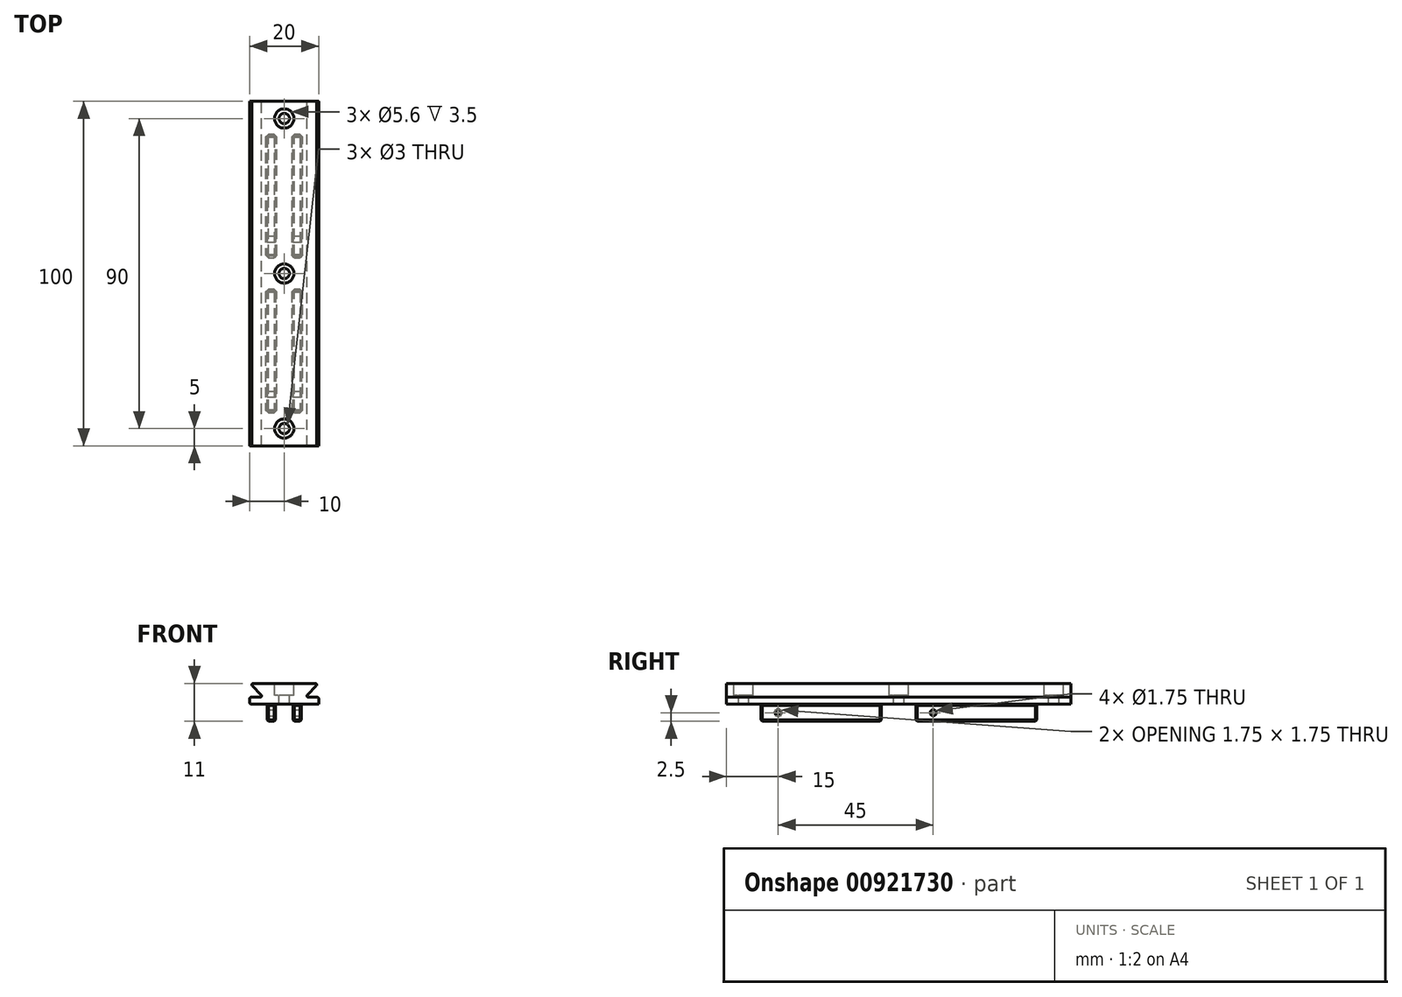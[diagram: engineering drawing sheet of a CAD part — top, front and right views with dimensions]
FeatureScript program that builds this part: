
annotation { "Feature Type Name" : "Feature", "Feature Type Description" : "" }
export const myFeature = defineFeature(function(context is Context, id is Id, definition is map)
    precondition{}
    {
        {
            var Q0;
            Q0=qCreatedBy(makeId("Front.planeOp"),FACE);
            var sketch = newSketch(context, id + "F0", { "sketchPlane" : qUnion([Q0])});
            skLineSegment(sketch, "E0.top", {"start": v(5, -2.5) * mm, "end": v(-5, -2.5) * mm});
            skLineSegment(sketch, "E0.left", {"start": v(5, 2.5) * mm, "end": v(5, -2.5) * mm});
            skLineSegment(sketch, "E0.right", {"start": v(-5, 2.5) * mm, "end": v(-5, -2.5) * mm});
            skPoint(sketch, "E0.middle", {"position": v(0, 0) * mm});
            skLineSegment(sketch, "E1.bottom", {"start": v(10, 4.5) * mm, "end": v(6, 4.5) * mm});
            skLineSegment(sketch, "E1.left", {"start": v(10, 4.5) * mm, "end": v(10, 2.5) * mm});
            skLineSegment(sketch, "E1.right", {"start": v(-10, 4.5) * mm, "end": v(-10, 2.5) * mm});
            skPoint(sketch, "E1.middle", {"position": v(0, 2.5) * mm});
            skLineSegment(sketch, "E2", {"start": v(-5, 2.5) * mm, "end": v(-10, 2.5) * mm});
            skLineSegment(sketch, "E3", {"start": v(5, 2.5) * mm, "end": v(10, 2.5) * mm});
            skPoint(sketch, "E4.orphan", {"position": v(-10, 0.5) * mm});
            skPoint(sketch, "E5.orphan", {"position": v(10, 0.5) * mm});
            skLineSegment(sketch, "E6.bottom", {"start": v(10, 8.5) * mm, "end": v(-10, 8.5) * mm});
            skPoint(sketch, "E6.middle", {"position": v(0, 4.5) * mm});
            skLineSegment(sketch, "E7.bottom", {"start": v(-10, 8.5) * mm, "end": v(-6, 8.5) * mm});
            skLineSegment(sketch, "E7.top", {"start": v(-10, 4.5) * mm, "end": v(-6, 4.5) * mm});
            skLineSegment(sketch, "E8.bottom", {"start": v(10, 8.5) * mm, "end": v(6, 8.5) * mm});
            skLineSegment(sketch, "E9", {"start": v(-10, 8.5) * mm, "end": v(-6, 4.5) * mm});
            skLineSegment(sketch, "E10", {"start": v(10, 8.5) * mm, "end": v(6, 4.5) * mm});
            skLineSegment(sketch, "E11.trimOffspring", {"start": v(-6, 4.5) * mm, "end": v(-10, 4.5) * mm});
            skLineSegment(sketch, "E12.bottom", {"start": v(-2.5, -2.5) * mm, "end": v(2.5, -2.5) * mm});
            skLineSegment(sketch, "E12.top", {"start": v(-2.5, 2.5) * mm, "end": v(2.5, 2.5) * mm});
            skLineSegment(sketch, "E12.left", {"start": v(-2.5, -2.5) * mm, "end": v(-2.5, 2.5) * mm});
            skLineSegment(sketch, "E12.right", {"start": v(2.5, -2.5) * mm, "end": v(2.5, 2.5) * mm});
            skSolve(sketch);
        }
        {
            var Q0;
            {var subQ0=sQuery(id+"F0.wireOp",EDGE,"E0.left");Q0=makeQuery(id+"F0.imprint","IMPRINT",FACE,{"disambiguationData":[TD([[makeQuery(id+"F0.imprint","IMPRINT",EDGE,{"derivedFrom":subQ0}),-1.0]])]});}
            extrude(context, id + "F1", {"entities" : qUnion([Q0]), "depth" : 100 * mm, "offsetDistance" : 25 * mm});
        }
        {
            var Q0;
            Q0=makeQuery(id+"F1.opExtrude","SWEPT_FACE",FACE,{"disambiguationData":[OSD([sQuery(id+"F0.wireOp",EDGE,"E12.top")])]});
            var sketch = newSketch(context, id + "F2", { "sketchPlane" : qUnion([Q0])});
            skLineSegment(sketch, "E13", {"start": v(-2.5, 10) * mm, "end": v(2.5, 10) * mm});
            skLineSegment(sketch, "E14", {"start": v(2.5, 90) * mm, "end": v(-2.5, 90) * mm});
            skLineSegment(sketch, "E15.top", {"start": v(-2.5, 55) * mm, "end": v(2.5, 55) * mm});
            skLineSegment(sketch, "E15.left", {"start": v(-2.5, 50) * mm, "end": v(-2.5, 55) * mm});
            skLineSegment(sketch, "E15.right", {"start": v(2.5, 50) * mm, "end": v(2.5, 55) * mm});
            skLineSegment(sketch, "E16.top", {"start": v(2.5, 45) * mm, "end": v(-2.5, 45) * mm});
            skLineSegment(sketch, "E16.left", {"start": v(2.5, 50) * mm, "end": v(2.5, 45) * mm});
            skLineSegment(sketch, "E16.right", {"start": v(-2.5, 50) * mm, "end": v(-2.5, 45) * mm});
            skSolve(sketch);
        }
        {
            var Q0;
            {var subQ0=sQuery(id+"F2.wireOp",EDGE,"E14");Q0=makeQuery(id+"F2.imprint","IMPRINT",FACE,{"disambiguationData":[TD([[makeQuery(id+"F2.imprint","IMPRINT",EDGE,{"derivedFrom":subQ0}),-1.0]])]});}
            var Q1;
            Q1=makeQuery(id+"F2.imprint","IMPRINT",FACE,{"disambiguationData":[TD([[makeQuery(id+"F2.imprint","IMPRINT",EDGE,{"derivedFrom":sQuery(id+"F2.wireOp",EDGE,"E15.top")}),-1.0]])]});
            var Q2;
            {var subQ0=sQuery(id+"F2.wireOp",EDGE,"E13");Q2=makeQuery(id+"F2.imprint","IMPRINT",FACE,{"disambiguationData":[TD([[makeQuery(id+"F2.imprint","IMPRINT",EDGE,{"derivedFrom":subQ0}),-1.0]])]});}
            extrude(context, id + "F3", {"entities" : qUnion([Q0, Q1, Q2]), "operationType" : NewBodyOperationType.ADD, "depth" : 5 * mm, "offsetDistance" : 25 * mm});
        }
        {
            var Q0;
            Q0=makeQuery(id+"F1.opExtrude","SWEPT_FACE",FACE,{"disambiguationData":[OSD([sQuery(id+"F0.wireOp",EDGE,"E0.left")])]});
            var sketch = newSketch(context, id + "F4", { "sketchPlane" : qUnion([Q0])});
            skLineSegment(sketch, "E17", {"start": v(-100, 2.5) * mm, "end": v(-100, -19) * mm});
            skLineSegment(sketch, "E18", {"start": v(-100, -19) * mm, "end": v(0, -19) * mm});
            skLineSegment(sketch, "E19", {"start": v(0, -19) * mm, "end": v(0, 2.5) * mm});
            skCircle(sketch, "E20", {"center": v(-85, 0) * mm, "radius": 0.87 * mm});
            skCircle(sketch, "E21", {"center": v(-40, 0) * mm, "radius": 0.87 * mm});
            skSolve(sketch);
        }
        {
            var Q0;
            Q0 = qSketchRegion(id + "F4", true);
            extrude(context, id + "F5", {"entities" : qUnion([Q0]), "operationType" : NewBodyOperationType.REMOVE, "oppositeDirection" : true, "depth" : 25 * mm, "offsetDistance" : 25 * mm});
        }
        {
            var Q0;
            Q0=makeQuery(id+"F1.opExtrude","SWEPT_EDGE",EDGE,{"disambiguationData":[OSD([sQuery(id+"F0.wireOp",EDGE,"E1.left"),sQuery(id+"F0.wireOp",EDGE,"E1.bottom")])]});
            var Q1;
            Q1=makeQuery(id+"F1.opExtrude","SWEPT_EDGE",EDGE,{"disambiguationData":[OSD([sQuery(id+"F0.wireOp",EDGE,"E1.right"),sQuery(id+"F0.wireOp",EDGE,"E11.trimOffspring")])]});
            var Q2;
            Q2=makeQuery(id+"F1.opExtrude","SWEPT_EDGE",EDGE,{"disambiguationData":[OSD([sQuery(id+"F0.wireOp",EDGE,"E9"),sQuery(id+"F0.wireOp",EDGE,"E11.trimOffspring")])]});
            var Q3;
            Q3=makeQuery(id+"F1.opExtrude","SWEPT_EDGE",EDGE,{"disambiguationData":[OSD([sQuery(id+"F0.wireOp",EDGE,"E1.bottom"),sQuery(id+"F0.wireOp",EDGE,"E10")])]});
            var Q4;
            Q4=makeQuery(id+"F1.opExtrude","SWEPT_EDGE",EDGE,{"disambiguationData":[OSD([sQuery(id+"F0.wireOp",EDGE,"E8.bottom"),sQuery(id+"F0.wireOp",EDGE,"E10")])]});
            var Q5;
            Q5=makeQuery(id+"F1.opExtrude","SWEPT_EDGE",EDGE,{"disambiguationData":[OSD([sQuery(id+"F0.wireOp",EDGE,"E7.bottom"),sQuery(id+"F0.wireOp",EDGE,"E9")])]});
            fillet(context, id + "F6", {"entities" : qUnion([Q0, Q1, Q2, Q3, Q4, Q5]), "radius" : 0.4 * mm, "tangentPropagation" : true, "allowEdgeOverflow" : false});
        }
        {
            var Q0;
            Q0=makeQuery(id+"F1.opExtrude","SWEPT_FACE",FACE,{"disambiguationData":[OSD([sQuery(id+"F0.wireOp",EDGE,"E6.bottom"),sQuery(id+"F0.wireOp",EDGE,"E7.bottom"),sQuery(id+"F0.wireOp",EDGE,"E8.bottom")])]});
            var sketch = newSketch(context, id + "F7", { "sketchPlane" : qUnion([Q0])});
            skLineSegment(sketch, "E22", {"start": v(0, -100) * mm, "end": v(0, -95) * mm});
            skLineSegment(sketch, "E23", {"start": v(0, 0) * mm, "end": v(0, -5) * mm});
            skLineSegment(sketch, "E24", {"start": v(0, -5) * mm, "end": v(0, -95) * mm});
            skCircle(sketch, "E25", {"center": v(0, -50) * mm, "radius": 2.8 * mm});
            skCircle(sketch, "E26", {"center": v(0, -5) * mm, "radius": 2.8 * mm});
            skCircle(sketch, "E27", {"center": v(0, -95) * mm, "radius": 2.8 * mm});
            skCircle(sketch, "E28", {"center": v(0, -5) * mm, "radius": 1.5 * mm});
            skCircle(sketch, "E29", {"center": v(0, -50) * mm, "radius": 1.5 * mm});
            skCircle(sketch, "E30", {"center": v(0, -95) * mm, "radius": 1.5 * mm});
            skSolve(sketch);
        }
        {
            var Q0;
            Q0 = qSketchRegion(id + "F7", true);
            extrude(context, id + "F8", {"entities" : qUnion([Q0]), "operationType" : NewBodyOperationType.REMOVE, "oppositeDirection" : true, "depth" : 3.5 * mm, "offsetDistance" : 25 * mm});
        }
        {
            var Q0;
            Q0=makeQuery(id+"F8.boolean.opBoolean","SPLIT",FACE,{"disambiguationData":[TD([makeQuery(id+"F8.opExtrude","SWEPT_FACE",FACE,{"disambiguationData":[OSD([sQuery(id+"F7.wireOp",EDGE,"E28")])]})])],"derivedFrom":makeQuery(id+"F1.opExtrude","SWEPT_FACE",FACE,{"disambiguationData":[OSD([sQuery(id+"F0.wireOp",EDGE,"E6.bottom"),sQuery(id+"F0.wireOp",EDGE,"E7.bottom"),sQuery(id+"F0.wireOp",EDGE,"E8.bottom")])]})});
            var Q1;
            Q1=makeQuery(id+"F8.boolean.opBoolean","SPLIT",FACE,{"disambiguationData":[TD([makeQuery(id+"F8.opExtrude","SWEPT_FACE",FACE,{"disambiguationData":[OSD([sQuery(id+"F7.wireOp",EDGE,"E29")])]})])],"derivedFrom":makeQuery(id+"F1.opExtrude","SWEPT_FACE",FACE,{"disambiguationData":[OSD([sQuery(id+"F0.wireOp",EDGE,"E6.bottom"),sQuery(id+"F0.wireOp",EDGE,"E7.bottom"),sQuery(id+"F0.wireOp",EDGE,"E8.bottom")])]})});
            var Q2;
            Q2=makeQuery(id+"F8.boolean.opBoolean","SPLIT",FACE,{"disambiguationData":[TD([makeQuery(id+"F8.opExtrude","SWEPT_FACE",FACE,{"disambiguationData":[OSD([sQuery(id+"F7.wireOp",EDGE,"E30")])]})])],"derivedFrom":makeQuery(id+"F1.opExtrude","SWEPT_FACE",FACE,{"disambiguationData":[OSD([sQuery(id+"F0.wireOp",EDGE,"E6.bottom"),sQuery(id+"F0.wireOp",EDGE,"E7.bottom"),sQuery(id+"F0.wireOp",EDGE,"E8.bottom")])]})});
            extrude(context, id + "F9", {"entities" : qUnion([Q0, Q1, Q2]), "operationType" : NewBodyOperationType.REMOVE, "endBound" : BoundingType.THROUGH_ALL, "oppositeDirection" : true, "depth" : 25 * mm, "offsetDistance" : 25 * mm});
        }
        {
            var Q0;
            Q0=makeQuery(id+"F8.boolean.opBoolean","COPY",EDGE,{"derivedFrom":makeQuery(id+"F8.opExtrude","CAP_EDGE",EDGE,{"disambiguationData":[OSD([sQuery(id+"F7.wireOp",EDGE,"E26")])],"isStart":true})});
            var Q1;
            Q1=makeQuery(id+"F8.boolean.opBoolean","COPY",EDGE,{"derivedFrom":makeQuery(id+"F8.opExtrude","CAP_EDGE",EDGE,{"disambiguationData":[OSD([sQuery(id+"F7.wireOp",EDGE,"E25")])],"isStart":true})});
            var Q2;
            Q2=makeQuery(id+"F8.boolean.opBoolean","COPY",EDGE,{"derivedFrom":makeQuery(id+"F8.opExtrude","CAP_EDGE",EDGE,{"disambiguationData":[OSD([sQuery(id+"F7.wireOp",EDGE,"E27")])],"isStart":true})});
            var Q3;
            Q3=makeQuery(id+"F8.boolean.opBoolean","COPY",EDGE,{"derivedFrom":makeQuery(id+"F8.opExtrude","CAP_EDGE",EDGE,{"disambiguationData":[OSD([sQuery(id+"F7.wireOp",EDGE,"E28")])],"isStart":false})});
            var Q4;
            Q4=makeQuery(id+"F8.boolean.opBoolean","COPY",EDGE,{"derivedFrom":makeQuery(id+"F8.opExtrude","CAP_EDGE",EDGE,{"disambiguationData":[OSD([sQuery(id+"F7.wireOp",EDGE,"E29")])],"isStart":false})});
            var Q5;
            Q5=makeQuery(id+"F8.boolean.opBoolean","COPY",EDGE,{"derivedFrom":makeQuery(id+"F8.opExtrude","CAP_EDGE",EDGE,{"disambiguationData":[OSD([sQuery(id+"F7.wireOp",EDGE,"E30")])],"isStart":false})});
            var Q6;
            {var subQ0=sQuery(id+"F0.wireOp",EDGE,"E12.right");var subQ1=sQuery(id+"F0.wireOp",EDGE,"E12.left");var subQ2=sQuery(id+"F0.wireOp",EDGE,"E12.top");var subQ3=sQuery(id+"F0.wireOp",EDGE,"E0.top");Q6=makeQuery(id+"F9.boolean.opBoolean","INTERSECT",EDGE,{"derivedFrom":[makeQuery(id+"F3.boolean.opBoolean","MERGE",FACE,{"derivedFrom":[makeQuery(id+"F1.opExtrude","SWEPT_FACE",FACE,{"disambiguationData":[OSD([subQ3]),TDD([makeQuery(id+"F0.imprint","IMPRINT",EDGE,{"disambiguationData":[TD([[makeQuery(id+"F0.imprint","INTERSECT",VERTEX,{"derivedFrom":[subQ3,sQuery(id+"F0.wireOp",EDGE,"E0.left")]}),-1.0]])],"derivedFrom":subQ3})])]}),makeQuery(id+"F1.opExtrude","SWEPT_FACE",FACE,{"disambiguationData":[OSD([subQ3]),TDD([makeQuery(id+"F0.imprint","IMPRINT",EDGE,{"disambiguationData":[TD([[makeQuery(id+"F0.imprint","INTERSECT",VERTEX,{"derivedFrom":[subQ3,sQuery(id+"F0.wireOp",EDGE,"E0.right")]}),1.0]])],"derivedFrom":subQ3})])]}),makeQuery(id+"F3.opExtrude","CAP_FACE",FACE,{"disambiguationData":[OSD([subQ2,subQ1,subQ0,sQuery(id+"F2.wireOp",EDGE,"E13")])],"isStart":false}),makeQuery(id+"F3.opExtrude","CAP_FACE",FACE,{"disambiguationData":[OSD([subQ2,subQ1,subQ0,sQuery(id+"F2.wireOp",EDGE,"E14")])],"isStart":false}),makeQuery(id+"F3.opExtrude","CAP_FACE",FACE,{"disambiguationData":[OSD([sQuery(id+"F2.wireOp",EDGE,"E15.top"),sQuery(id+"F2.wireOp",EDGE,"E15.left"),sQuery(id+"F2.wireOp",EDGE,"E15.right"),sQuery(id+"F2.wireOp",EDGE,"E16.top"),sQuery(id+"F2.wireOp",EDGE,"E16.left"),sQuery(id+"F2.wireOp",EDGE,"E16.right")])],"isStart":false})]}),makeQuery(id+"F9.opExtrude","SWEPT_FACE",FACE,{"disambiguationData":[OSD([sQuery(id+"F7.wireOp",EDGE,"E30")])]})]});}
            var Q7;
            {var subQ0=sQuery(id+"F0.wireOp",EDGE,"E12.right");var subQ1=sQuery(id+"F0.wireOp",EDGE,"E12.left");var subQ2=sQuery(id+"F0.wireOp",EDGE,"E12.top");var subQ3=sQuery(id+"F0.wireOp",EDGE,"E0.top");Q7=makeQuery(id+"F9.boolean.opBoolean","INTERSECT",EDGE,{"derivedFrom":[makeQuery(id+"F3.boolean.opBoolean","MERGE",FACE,{"derivedFrom":[makeQuery(id+"F1.opExtrude","SWEPT_FACE",FACE,{"disambiguationData":[OSD([subQ3]),TDD([makeQuery(id+"F0.imprint","IMPRINT",EDGE,{"disambiguationData":[TD([[makeQuery(id+"F0.imprint","INTERSECT",VERTEX,{"derivedFrom":[subQ3,sQuery(id+"F0.wireOp",EDGE,"E0.left")]}),-1.0]])],"derivedFrom":subQ3})])]}),makeQuery(id+"F1.opExtrude","SWEPT_FACE",FACE,{"disambiguationData":[OSD([subQ3]),TDD([makeQuery(id+"F0.imprint","IMPRINT",EDGE,{"disambiguationData":[TD([[makeQuery(id+"F0.imprint","INTERSECT",VERTEX,{"derivedFrom":[subQ3,sQuery(id+"F0.wireOp",EDGE,"E0.right")]}),1.0]])],"derivedFrom":subQ3})])]}),makeQuery(id+"F3.opExtrude","CAP_FACE",FACE,{"disambiguationData":[OSD([subQ2,subQ1,subQ0,sQuery(id+"F2.wireOp",EDGE,"E13")])],"isStart":false}),makeQuery(id+"F3.opExtrude","CAP_FACE",FACE,{"disambiguationData":[OSD([subQ2,subQ1,subQ0,sQuery(id+"F2.wireOp",EDGE,"E14")])],"isStart":false}),makeQuery(id+"F3.opExtrude","CAP_FACE",FACE,{"disambiguationData":[OSD([sQuery(id+"F2.wireOp",EDGE,"E15.top"),sQuery(id+"F2.wireOp",EDGE,"E15.left"),sQuery(id+"F2.wireOp",EDGE,"E15.right"),sQuery(id+"F2.wireOp",EDGE,"E16.top"),sQuery(id+"F2.wireOp",EDGE,"E16.left"),sQuery(id+"F2.wireOp",EDGE,"E16.right")])],"isStart":false})]}),makeQuery(id+"F9.opExtrude","SWEPT_FACE",FACE,{"disambiguationData":[OSD([sQuery(id+"F7.wireOp",EDGE,"E29")])]})]});}
            var Q8;
            {var subQ0=sQuery(id+"F0.wireOp",EDGE,"E12.right");var subQ1=sQuery(id+"F0.wireOp",EDGE,"E12.left");var subQ2=sQuery(id+"F0.wireOp",EDGE,"E12.top");var subQ3=sQuery(id+"F0.wireOp",EDGE,"E0.top");Q8=makeQuery(id+"F9.boolean.opBoolean","INTERSECT",EDGE,{"derivedFrom":[makeQuery(id+"F3.boolean.opBoolean","MERGE",FACE,{"derivedFrom":[makeQuery(id+"F1.opExtrude","SWEPT_FACE",FACE,{"disambiguationData":[OSD([subQ3]),TDD([makeQuery(id+"F0.imprint","IMPRINT",EDGE,{"disambiguationData":[TD([[makeQuery(id+"F0.imprint","INTERSECT",VERTEX,{"derivedFrom":[subQ3,sQuery(id+"F0.wireOp",EDGE,"E0.left")]}),-1.0]])],"derivedFrom":subQ3})])]}),makeQuery(id+"F1.opExtrude","SWEPT_FACE",FACE,{"disambiguationData":[OSD([subQ3]),TDD([makeQuery(id+"F0.imprint","IMPRINT",EDGE,{"disambiguationData":[TD([[makeQuery(id+"F0.imprint","INTERSECT",VERTEX,{"derivedFrom":[subQ3,sQuery(id+"F0.wireOp",EDGE,"E0.right")]}),1.0]])],"derivedFrom":subQ3})])]}),makeQuery(id+"F3.opExtrude","CAP_FACE",FACE,{"disambiguationData":[OSD([subQ2,subQ1,subQ0,sQuery(id+"F2.wireOp",EDGE,"E13")])],"isStart":false}),makeQuery(id+"F3.opExtrude","CAP_FACE",FACE,{"disambiguationData":[OSD([subQ2,subQ1,subQ0,sQuery(id+"F2.wireOp",EDGE,"E14")])],"isStart":false}),makeQuery(id+"F3.opExtrude","CAP_FACE",FACE,{"disambiguationData":[OSD([sQuery(id+"F2.wireOp",EDGE,"E15.top"),sQuery(id+"F2.wireOp",EDGE,"E15.left"),sQuery(id+"F2.wireOp",EDGE,"E15.right"),sQuery(id+"F2.wireOp",EDGE,"E16.top"),sQuery(id+"F2.wireOp",EDGE,"E16.left"),sQuery(id+"F2.wireOp",EDGE,"E16.right")])],"isStart":false})]}),makeQuery(id+"F9.opExtrude","SWEPT_FACE",FACE,{"disambiguationData":[OSD([sQuery(id+"F7.wireOp",EDGE,"E28")])]})]});}
            chamfer(context, id + "F10", {"entities" : qUnion([Q0, Q1, Q2, Q3, Q4, Q5, Q6, Q7, Q8]), "width" : 0.5 * mm, "tangentPropagation" : true});
        }
        {
            var Q0;
            Q0=makeQuery(id+"F1.opExtrude","SWEPT_FACE",FACE,{"disambiguationData":[OSD([sQuery(id+"F0.wireOp",EDGE,"E0.right")])]});
            var sketch = newSketch(context, id + "F11", { "sketchPlane" : qUnion([Q0])});
            skLineSegment(sketch, "E31.bottom", {"start": v(0, 2.5) * mm, "end": v(10, 2.5) * mm});
            skLineSegment(sketch, "E31.top", {"start": v(0, -2.5) * mm, "end": v(10, -2.5) * mm});
            skLineSegment(sketch, "E31.left", {"start": v(0, 2.5) * mm, "end": v(0, -2.5) * mm});
            skLineSegment(sketch, "E31.right", {"start": v(10, 2.5) * mm, "end": v(10, -2.5) * mm});
            skLineSegment(sketch, "E32.bottom", {"start": v(45, 2.5) * mm, "end": v(55, 2.5) * mm});
            skLineSegment(sketch, "E32.top", {"start": v(45, -2.5) * mm, "end": v(55, -2.5) * mm});
            skLineSegment(sketch, "E32.left", {"start": v(45, 2.5) * mm, "end": v(45, -2.5) * mm});
            skLineSegment(sketch, "E32.right", {"start": v(55, 2.5) * mm, "end": v(55, -2.5) * mm});
            skLineSegment(sketch, "E33.bottom", {"start": v(100, 2.5) * mm, "end": v(90, 2.5) * mm});
            skLineSegment(sketch, "E33.top", {"start": v(100, -2.5) * mm, "end": v(90, -2.5) * mm});
            skLineSegment(sketch, "E33.left", {"start": v(100, 2.5) * mm, "end": v(100, -2.5) * mm});
            skLineSegment(sketch, "E33.right", {"start": v(90, 2.5) * mm, "end": v(90, -2.5) * mm});
            skSolve(sketch);
        }
        {
            var Q0;
            Q0 = qSketchRegion(id + "F11", true);
            extrude(context, id + "F12", {"entities" : qUnion([Q0]), "operationType" : NewBodyOperationType.REMOVE, "oppositeDirection" : true, "depth" : 25 * mm, "offsetDistance" : 25 * mm});
        }
        {
            var Q0;
            {var subQ0=sQuery(id+"F0.wireOp",EDGE,"E0.left");var subQ1=sQuery(id+"F0.wireOp",EDGE,"E12.right");var subQ2=sQuery(id+"F0.wireOp",EDGE,"E12.left");var subQ3=sQuery(id+"F0.wireOp",EDGE,"E12.top");var subQ4=sQuery(id+"F0.wireOp",EDGE,"E0.top");Q0=makeQuery(id+"F12.boolean.opBoolean","SPLIT",FACE,{"disambiguationData":[TD([makeQuery(id+"F1.opExtrude","SWEPT_FACE",FACE,{"disambiguationData":[OSD([subQ0])]}),makeQuery(id+"F1.opExtrude","SWEPT_FACE",FACE,{"disambiguationData":[OSD([subQ1])]}),makeQuery(id+"F12.opExtrude","SWEPT_FACE",FACE,{"disambiguationData":[OSD([sQuery(id+"F11.wireOp",EDGE,"E32.right")])]}),makeQuery(id+"F12.opExtrude","SWEPT_FACE",FACE,{"disambiguationData":[OSD([sQuery(id+"F11.wireOp",EDGE,"E33.right")])]})])],"derivedFrom":makeQuery(id+"F3.boolean.opBoolean","MERGE",FACE,{"derivedFrom":[makeQuery(id+"F1.opExtrude","SWEPT_FACE",FACE,{"disambiguationData":[OSD([subQ4]),TDD([makeQuery(id+"F0.imprint","IMPRINT",EDGE,{"disambiguationData":[TD([[makeQuery(id+"F0.imprint","INTERSECT",VERTEX,{"derivedFrom":[subQ4,subQ0]}),-1.0]])],"derivedFrom":subQ4})])]}),makeQuery(id+"F1.opExtrude","SWEPT_FACE",FACE,{"disambiguationData":[OSD([subQ4]),TDD([makeQuery(id+"F0.imprint","IMPRINT",EDGE,{"disambiguationData":[TD([[makeQuery(id+"F0.imprint","INTERSECT",VERTEX,{"derivedFrom":[subQ4,sQuery(id+"F0.wireOp",EDGE,"E0.right")]}),1.0]])],"derivedFrom":subQ4})])]}),makeQuery(id+"F3.opExtrude","CAP_FACE",FACE,{"disambiguationData":[OSD([subQ3,subQ2,subQ1,sQuery(id+"F2.wireOp",EDGE,"E13")])],"isStart":false}),makeQuery(id+"F3.opExtrude","CAP_FACE",FACE,{"disambiguationData":[OSD([subQ3,subQ2,subQ1,sQuery(id+"F2.wireOp",EDGE,"E14")])],"isStart":false}),makeQuery(id+"F3.opExtrude","CAP_FACE",FACE,{"disambiguationData":[OSD([sQuery(id+"F2.wireOp",EDGE,"E15.top"),sQuery(id+"F2.wireOp",EDGE,"E15.left"),sQuery(id+"F2.wireOp",EDGE,"E15.right"),sQuery(id+"F2.wireOp",EDGE,"E16.top"),sQuery(id+"F2.wireOp",EDGE,"E16.left"),sQuery(id+"F2.wireOp",EDGE,"E16.right")])],"isStart":false})]})});}
            var Q1;
            {var subQ0=sQuery(id+"F0.wireOp",EDGE,"E0.right");var subQ1=sQuery(id+"F0.wireOp",EDGE,"E12.left");var subQ2=sQuery(id+"F0.wireOp",EDGE,"E12.right");var subQ3=sQuery(id+"F0.wireOp",EDGE,"E12.top");var subQ4=sQuery(id+"F0.wireOp",EDGE,"E0.top");Q1=makeQuery(id+"F12.boolean.opBoolean","SPLIT",FACE,{"disambiguationData":[TD([makeQuery(id+"F1.opExtrude","SWEPT_FACE",FACE,{"disambiguationData":[OSD([subQ0])]}),makeQuery(id+"F1.opExtrude","SWEPT_FACE",FACE,{"disambiguationData":[OSD([subQ1])]}),makeQuery(id+"F12.opExtrude","SWEPT_FACE",FACE,{"disambiguationData":[OSD([sQuery(id+"F11.wireOp",EDGE,"E32.right")])]}),makeQuery(id+"F12.opExtrude","SWEPT_FACE",FACE,{"disambiguationData":[OSD([sQuery(id+"F11.wireOp",EDGE,"E33.right")])]})])],"derivedFrom":makeQuery(id+"F3.boolean.opBoolean","MERGE",FACE,{"derivedFrom":[makeQuery(id+"F1.opExtrude","SWEPT_FACE",FACE,{"disambiguationData":[OSD([subQ4]),TDD([makeQuery(id+"F0.imprint","IMPRINT",EDGE,{"disambiguationData":[TD([[makeQuery(id+"F0.imprint","INTERSECT",VERTEX,{"derivedFrom":[subQ4,sQuery(id+"F0.wireOp",EDGE,"E0.left")]}),-1.0]])],"derivedFrom":subQ4})])]}),makeQuery(id+"F1.opExtrude","SWEPT_FACE",FACE,{"disambiguationData":[OSD([subQ4]),TDD([makeQuery(id+"F0.imprint","IMPRINT",EDGE,{"disambiguationData":[TD([[makeQuery(id+"F0.imprint","INTERSECT",VERTEX,{"derivedFrom":[subQ4,subQ0]}),1.0]])],"derivedFrom":subQ4})])]}),makeQuery(id+"F3.opExtrude","CAP_FACE",FACE,{"disambiguationData":[OSD([subQ3,subQ1,subQ2,sQuery(id+"F2.wireOp",EDGE,"E13")])],"isStart":false}),makeQuery(id+"F3.opExtrude","CAP_FACE",FACE,{"disambiguationData":[OSD([subQ3,subQ1,subQ2,sQuery(id+"F2.wireOp",EDGE,"E14")])],"isStart":false}),makeQuery(id+"F3.opExtrude","CAP_FACE",FACE,{"disambiguationData":[OSD([sQuery(id+"F2.wireOp",EDGE,"E15.top"),sQuery(id+"F2.wireOp",EDGE,"E15.left"),sQuery(id+"F2.wireOp",EDGE,"E15.right"),sQuery(id+"F2.wireOp",EDGE,"E16.top"),sQuery(id+"F2.wireOp",EDGE,"E16.left"),sQuery(id+"F2.wireOp",EDGE,"E16.right")])],"isStart":false})]})});}
            var Q2;
            {var subQ0=sQuery(id+"F0.wireOp",EDGE,"E0.right");var subQ1=sQuery(id+"F0.wireOp",EDGE,"E12.left");var subQ2=sQuery(id+"F0.wireOp",EDGE,"E12.right");var subQ3=sQuery(id+"F0.wireOp",EDGE,"E12.top");var subQ4=sQuery(id+"F0.wireOp",EDGE,"E0.top");Q2=makeQuery(id+"F12.boolean.opBoolean","SPLIT",FACE,{"disambiguationData":[TD([makeQuery(id+"F1.opExtrude","SWEPT_FACE",FACE,{"disambiguationData":[OSD([subQ0])]}),makeQuery(id+"F1.opExtrude","SWEPT_FACE",FACE,{"disambiguationData":[OSD([subQ1])]}),makeQuery(id+"F12.opExtrude","SWEPT_FACE",FACE,{"disambiguationData":[OSD([sQuery(id+"F11.wireOp",EDGE,"E31.right")])]}),makeQuery(id+"F12.opExtrude","SWEPT_FACE",FACE,{"disambiguationData":[OSD([sQuery(id+"F11.wireOp",EDGE,"E32.left")])]})])],"derivedFrom":makeQuery(id+"F3.boolean.opBoolean","MERGE",FACE,{"derivedFrom":[makeQuery(id+"F1.opExtrude","SWEPT_FACE",FACE,{"disambiguationData":[OSD([subQ4]),TDD([makeQuery(id+"F0.imprint","IMPRINT",EDGE,{"disambiguationData":[TD([[makeQuery(id+"F0.imprint","INTERSECT",VERTEX,{"derivedFrom":[subQ4,sQuery(id+"F0.wireOp",EDGE,"E0.left")]}),-1.0]])],"derivedFrom":subQ4})])]}),makeQuery(id+"F1.opExtrude","SWEPT_FACE",FACE,{"disambiguationData":[OSD([subQ4]),TDD([makeQuery(id+"F0.imprint","IMPRINT",EDGE,{"disambiguationData":[TD([[makeQuery(id+"F0.imprint","INTERSECT",VERTEX,{"derivedFrom":[subQ4,subQ0]}),1.0]])],"derivedFrom":subQ4})])]}),makeQuery(id+"F3.opExtrude","CAP_FACE",FACE,{"disambiguationData":[OSD([subQ3,subQ1,subQ2,sQuery(id+"F2.wireOp",EDGE,"E13")])],"isStart":false}),makeQuery(id+"F3.opExtrude","CAP_FACE",FACE,{"disambiguationData":[OSD([subQ3,subQ1,subQ2,sQuery(id+"F2.wireOp",EDGE,"E14")])],"isStart":false}),makeQuery(id+"F3.opExtrude","CAP_FACE",FACE,{"disambiguationData":[OSD([sQuery(id+"F2.wireOp",EDGE,"E15.top"),sQuery(id+"F2.wireOp",EDGE,"E15.left"),sQuery(id+"F2.wireOp",EDGE,"E15.right"),sQuery(id+"F2.wireOp",EDGE,"E16.top"),sQuery(id+"F2.wireOp",EDGE,"E16.left"),sQuery(id+"F2.wireOp",EDGE,"E16.right")])],"isStart":false})]})});}
            var Q3;
            {var subQ0=sQuery(id+"F0.wireOp",EDGE,"E0.left");var subQ1=sQuery(id+"F0.wireOp",EDGE,"E12.right");var subQ2=sQuery(id+"F0.wireOp",EDGE,"E12.left");var subQ3=sQuery(id+"F0.wireOp",EDGE,"E12.top");var subQ4=sQuery(id+"F0.wireOp",EDGE,"E0.top");Q3=makeQuery(id+"F12.boolean.opBoolean","SPLIT",FACE,{"disambiguationData":[TD([makeQuery(id+"F1.opExtrude","SWEPT_FACE",FACE,{"disambiguationData":[OSD([subQ0])]}),makeQuery(id+"F1.opExtrude","SWEPT_FACE",FACE,{"disambiguationData":[OSD([subQ1])]}),makeQuery(id+"F12.opExtrude","SWEPT_FACE",FACE,{"disambiguationData":[OSD([sQuery(id+"F11.wireOp",EDGE,"E31.right")])]}),makeQuery(id+"F12.opExtrude","SWEPT_FACE",FACE,{"disambiguationData":[OSD([sQuery(id+"F11.wireOp",EDGE,"E32.left")])]})])],"derivedFrom":makeQuery(id+"F3.boolean.opBoolean","MERGE",FACE,{"derivedFrom":[makeQuery(id+"F1.opExtrude","SWEPT_FACE",FACE,{"disambiguationData":[OSD([subQ4]),TDD([makeQuery(id+"F0.imprint","IMPRINT",EDGE,{"disambiguationData":[TD([[makeQuery(id+"F0.imprint","INTERSECT",VERTEX,{"derivedFrom":[subQ4,subQ0]}),-1.0]])],"derivedFrom":subQ4})])]}),makeQuery(id+"F1.opExtrude","SWEPT_FACE",FACE,{"disambiguationData":[OSD([subQ4]),TDD([makeQuery(id+"F0.imprint","IMPRINT",EDGE,{"disambiguationData":[TD([[makeQuery(id+"F0.imprint","INTERSECT",VERTEX,{"derivedFrom":[subQ4,sQuery(id+"F0.wireOp",EDGE,"E0.right")]}),1.0]])],"derivedFrom":subQ4})])]}),makeQuery(id+"F3.opExtrude","CAP_FACE",FACE,{"disambiguationData":[OSD([subQ3,subQ2,subQ1,sQuery(id+"F2.wireOp",EDGE,"E13")])],"isStart":false}),makeQuery(id+"F3.opExtrude","CAP_FACE",FACE,{"disambiguationData":[OSD([subQ3,subQ2,subQ1,sQuery(id+"F2.wireOp",EDGE,"E14")])],"isStart":false}),makeQuery(id+"F3.opExtrude","CAP_FACE",FACE,{"disambiguationData":[OSD([sQuery(id+"F2.wireOp",EDGE,"E15.top"),sQuery(id+"F2.wireOp",EDGE,"E15.left"),sQuery(id+"F2.wireOp",EDGE,"E15.right"),sQuery(id+"F2.wireOp",EDGE,"E16.top"),sQuery(id+"F2.wireOp",EDGE,"E16.left"),sQuery(id+"F2.wireOp",EDGE,"E16.right")])],"isStart":false})]})});}
            var Q4;
            {var subQ0=sQuery(id+"F0.wireOp",EDGE,"E0.left");Q4=makeQuery(id+"F12.boolean.opBoolean","COPY",FACE,{"disambiguationData":[TD([makeQuery(id+"F1.opExtrude","SWEPT_FACE",FACE,{"disambiguationData":[OSD([subQ0])]})])],"derivedFrom":makeQuery(id+"F12.opExtrude","SWEPT_FACE",FACE,{"disambiguationData":[OSD([sQuery(id+"F11.wireOp",EDGE,"E33.right")])]})});}
            var Q5;
            {var subQ5=sQuery(id+"F0.wireOp",EDGE,"E0.right");Q5=makeQuery(id+"F12.boolean.opBoolean","COPY",FACE,{"disambiguationData":[TD([makeQuery(id+"F1.opExtrude","SWEPT_FACE",FACE,{"disambiguationData":[OSD([subQ5])]})])],"derivedFrom":makeQuery(id+"F12.opExtrude","SWEPT_FACE",FACE,{"disambiguationData":[OSD([sQuery(id+"F11.wireOp",EDGE,"E33.right")])]})});}
            var Q6;
            {var subQ0=sQuery(id+"F0.wireOp",EDGE,"E0.left");Q6=makeQuery(id+"F12.boolean.opBoolean","COPY",FACE,{"disambiguationData":[TD([makeQuery(id+"F1.opExtrude","SWEPT_FACE",FACE,{"disambiguationData":[OSD([subQ0])]})])],"derivedFrom":makeQuery(id+"F12.opExtrude","SWEPT_FACE",FACE,{"disambiguationData":[OSD([sQuery(id+"F11.wireOp",EDGE,"E32.left")])]})});}
            var Q7;
            {var subQ5=sQuery(id+"F0.wireOp",EDGE,"E0.right");Q7=makeQuery(id+"F12.boolean.opBoolean","COPY",FACE,{"disambiguationData":[TD([makeQuery(id+"F1.opExtrude","SWEPT_FACE",FACE,{"disambiguationData":[OSD([subQ5])]})])],"derivedFrom":makeQuery(id+"F12.opExtrude","SWEPT_FACE",FACE,{"disambiguationData":[OSD([sQuery(id+"F11.wireOp",EDGE,"E32.left")])]})});}
            var Q8;
            {var subQ0=sQuery(id+"F0.wireOp",EDGE,"E0.left");Q8=makeQuery(id+"F12.boolean.opBoolean","COPY",FACE,{"disambiguationData":[TD([makeQuery(id+"F1.opExtrude","SWEPT_FACE",FACE,{"disambiguationData":[OSD([subQ0])]})])],"derivedFrom":makeQuery(id+"F12.opExtrude","SWEPT_FACE",FACE,{"disambiguationData":[OSD([sQuery(id+"F11.wireOp",EDGE,"E32.right")])]})});}
            var Q9;
            {var subQ5=sQuery(id+"F0.wireOp",EDGE,"E0.right");Q9=makeQuery(id+"F12.boolean.opBoolean","COPY",FACE,{"disambiguationData":[TD([makeQuery(id+"F1.opExtrude","SWEPT_FACE",FACE,{"disambiguationData":[OSD([subQ5])]})])],"derivedFrom":makeQuery(id+"F12.opExtrude","SWEPT_FACE",FACE,{"disambiguationData":[OSD([sQuery(id+"F11.wireOp",EDGE,"E32.right")])]})});}
            var Q10;
            {var subQ5=sQuery(id+"F0.wireOp",EDGE,"E0.right");Q10=makeQuery(id+"F12.boolean.opBoolean","COPY",FACE,{"disambiguationData":[TD([makeQuery(id+"F1.opExtrude","SWEPT_FACE",FACE,{"disambiguationData":[OSD([subQ5])]})])],"derivedFrom":makeQuery(id+"F12.opExtrude","SWEPT_FACE",FACE,{"disambiguationData":[OSD([sQuery(id+"F11.wireOp",EDGE,"E31.right")])]})});}
            var Q11;
            {var subQ0=sQuery(id+"F0.wireOp",EDGE,"E0.left");Q11=makeQuery(id+"F12.boolean.opBoolean","COPY",FACE,{"disambiguationData":[TD([makeQuery(id+"F1.opExtrude","SWEPT_FACE",FACE,{"disambiguationData":[OSD([subQ0])]})])],"derivedFrom":makeQuery(id+"F12.opExtrude","SWEPT_FACE",FACE,{"disambiguationData":[OSD([sQuery(id+"F11.wireOp",EDGE,"E31.right")])]})});}
            chamfer(context, id + "F13", {"entities" : qUnion([Q0, Q1, Q2, Q3, Q4, Q5, Q6, Q7, Q8, Q9, Q10, Q11]), "width" : 0.4 * mm, "tangentPropagation" : true});
        }
    });
